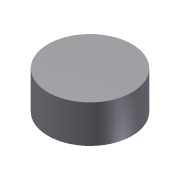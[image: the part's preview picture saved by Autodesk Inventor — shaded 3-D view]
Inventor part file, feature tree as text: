
AUTODESK INVENTOR PART (.ipt)
format: ipt  version: 2012 (Build 160160000, 160)  size: 66,048 bytes
history: native  units: mm
features: extrude x1, sketch x1, reference x1
ambient origin geometry x8: Origin, YZ Plane, XZ Plane, XY Plane, X Axis, Y Axis, Z Axis, Center Point
bodies: Solid1 (feature_tree)
feature tree (3):
  extrude  "Extrusion1"  [1 undecoded]
  sketch  "Sketch1"  dims[d0=9.0mm d1=0.0mm]
  reference  "Reference1"
note: 1 required parameter value undecoded (feature->parameter linkage not recoverable at this tier; creation-order binding heuristic only, values carry confidence <= 0.55)
